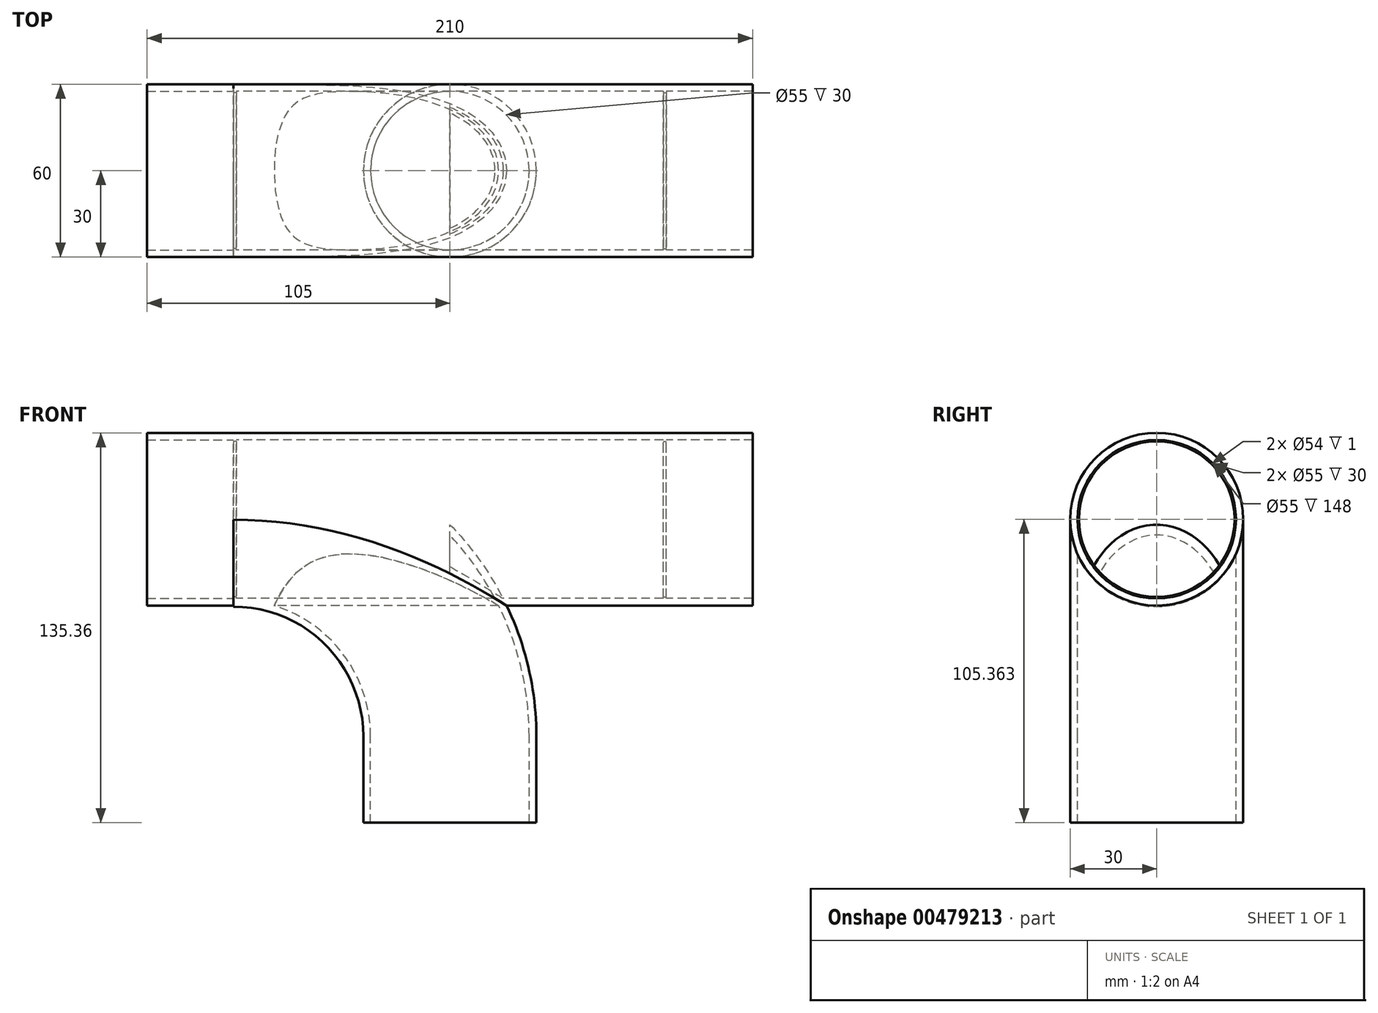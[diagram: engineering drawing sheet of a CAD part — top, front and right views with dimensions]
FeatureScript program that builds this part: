
annotation { "Feature Type Name" : "Feature", "Feature Type Description" : "" }
export const myFeature = defineFeature(function(context is Context, id is Id, definition is map)
    precondition{}
    {
        {
            var Q0;
            Q0=qCreatedBy(makeId("Top.planeOp"),FACE);
            var sketch = newSketch(context, id + "F0", { "sketchPlane" : qUnion([Q0])});
            skCircle(sketch, "E0", {"center": v(0, 0) * mm, "radius": 27.5 * mm});
            skCircle(sketch, "E1", {"center": v(0, 0) * mm, "radius": 30 * mm});
            skSolve(sketch);
        }
        {
            var Q0;
            Q0=qCreatedBy(makeId("Front.planeOp"),FACE);
            var sketch = newSketch(context, id + "F1", { "sketchPlane" : qUnion([Q0])});
            skArc(sketch, "E2", {"start": v(75, 75) * mm, "mid": v(21.97, 53.03) * mm, "end": v(0, 0) * mm});
            skLineSegment(sketch, "E3", {"start": v(0, 0) * mm, "end": v(75, 0) * mm});
            skLineSegment(sketch, "E4", {"start": v(75, 0) * mm, "end": v(75, 75) * mm});
            skLineSegment(sketch, "E5", {"start": v(0, 0) * mm, "end": v(-75, 0) * mm});
            skArc(sketch, "E6", {"start": v(0, 0) * mm, "mid": v(-21.97, 53.03) * mm, "end": v(-75, 75) * mm});
            skLineSegment(sketch, "E7", {"start": v(-75, 0) * mm, "end": v(-75, 75) * mm});
            skLineSegment(sketch, "E8", {"start": v(-75, 75) * mm, "end": v(75, 75) * mm});
            skSolve(sketch);
        }
        {
            var Q0;
            Q0=makeQuery(id+"F0.imprint","IMPRINT",FACE,{"disambiguationData":[TD([[makeQuery(id+"F0.imprint","IMPRINT",EDGE,{"derivedFrom":sQuery(id+"F0.wireOp",EDGE,"E0")}),-1.0]])]});
            var Q1;
            Q1=sQuery(id+"F1.wireOp",EDGE,"E6");
            sweep(context, id + "F2", {"profiles" : qUnion([Q0]), "path" : qUnion([Q1])});
        }
        {
            var Q0;
            Q0=qCreatedBy(makeId("Right.planeOp"),FACE);
            var sketch = newSketch(context, id + "F3", { "sketchPlane" : qUnion([Q0])});
            skCircle(sketch, "E9", {"center": v(0, 75.36) * mm, "radius": 30 * mm});
            skCircle(sketch, "E10", {"center": v(0, 75.36) * mm, "radius": 27.5 * mm});
            skSolve(sketch);
        }
        {
            var Q0;
            Q0=makeQuery(id+"F3.imprint","IMPRINT",FACE,{"disambiguationData":[TD([[makeQuery(id+"F3.imprint","IMPRINT",EDGE,{"derivedFrom":sQuery(id+"F3.wireOp",EDGE,"E9")}),1.0]])]});
            extrude(context, id + "F4", {"entities" : qUnion([Q0]), "operationType" : NewBodyOperationType.ADD, "depth" : 150 * mm, "offsetDistance" : 25 * mm, "symmetric" : true});
        }
        {
            var Q0;
            Q0=makeQuery(id+"F3.imprint","IMPRINT",FACE,{"disambiguationData":[TD([[makeQuery(id+"F3.imprint","IMPRINT",EDGE,{"derivedFrom":sQuery(id+"F3.wireOp",EDGE,"E10")}),1.0]])]});
            extrude(context, id + "F5", {"entities" : qUnion([Q0]), "operationType" : NewBodyOperationType.REMOVE, "oppositeDirection" : true, "depth" : 115 * mm, "offsetDistance" : 25 * mm});
        }
        {
            var Q0;
            Q0=makeQuery(id+"F2.opSweep","CAP_FACE",FACE,{"disambiguationData":[OSD([sQuery(id+"F0.wireOp",EDGE,"E0"),sQuery(id+"F0.wireOp",EDGE,"E1"),sQuery(id+"F1.wireOp",VERTEX,"E6.start")])],"isStart":true});
            extrude(context, id + "F6", {"entities" : qUnion([Q0]), "operationType" : NewBodyOperationType.ADD, "depth" : 30 * mm, "offsetDistance" : 25 * mm});
        }
        {
            var Q0;
            Q0=makeQuery(id+"F4.opExtrude","CAP_FACE",FACE,{"disambiguationData":[OSD([sQuery(id+"F3.wireOp",EDGE,"E9"),sQuery(id+"F3.wireOp",EDGE,"E10")])],"isStart":false});
            var sketch = newSketch(context, id + "F7", { "sketchPlane" : qUnion([Q0])});
            skCircle(sketch, "E11", {"center": v(0, 75.36) * mm, "radius": 27.5 * mm});
            skCircle(sketch, "E12", {"center": v(0, 75.36) * mm, "radius": 27 * mm});
            skSolve(sketch);
        }
        {
            var Q0;
            Q0=makeQuery(id+"F7.imprint","IMPRINT",FACE,{"disambiguationData":[TD([[makeQuery(id+"F7.imprint","IMPRINT",EDGE,{"derivedFrom":sQuery(id+"F7.wireOp",EDGE,"E11")}),1.0]])]});
            extrude(context, id + "F8", {"entities" : qUnion([Q0]), "operationType" : NewBodyOperationType.ADD, "oppositeDirection" : true, "depth" : 1 * mm, "offsetDistance" : 25 * mm});
        }
        {
            var Q0;
            Q0=makeQuery(id+"F8.boolean.opBoolean","MERGE",FACE,{"derivedFrom":[makeQuery(id+"F4.opExtrude","CAP_FACE",FACE,{"disambiguationData":[OSD([sQuery(id+"F3.wireOp",EDGE,"E9"),sQuery(id+"F3.wireOp",EDGE,"E10")])],"isStart":false}),makeQuery(id+"F8.opExtrude","CAP_FACE",FACE,{"disambiguationData":[OSD([sQuery(id+"F7.wireOp",EDGE,"E11"),sQuery(id+"F7.wireOp",EDGE,"E12")])],"isStart":true})]});
            var sketch = newSketch(context, id + "F9", { "sketchPlane" : qUnion([Q0])});
            skCircle(sketch, "E13", {"center": v(0, 75.36) * mm, "radius": 27.5 * mm});
            skCircle(sketch, "E14", {"center": v(0, 75.36) * mm, "radius": 30 * mm});
            skSolve(sketch);
        }
        {
            var Q0;
            Q0=makeQuery(id+"F9.imprint","IMPRINT",FACE,{"disambiguationData":[TD([[makeQuery(id+"F9.imprint","IMPRINT",EDGE,{"derivedFrom":sQuery(id+"F9.wireOp",EDGE,"E13")}),-1.0]])]});
            extrude(context, id + "F10", {"entities" : qUnion([Q0]), "operationType" : NewBodyOperationType.ADD, "depth" : 30 * mm, "offsetDistance" : 25 * mm});
        }
        {
            var Q0;
            Q0=makeQuery(id+"F4.boolean.opBoolean","MERGE",FACE,{"derivedFrom":[makeQuery(id+"F2.opSweep","CAP_FACE",FACE,{"disambiguationData":[OSD([sQuery(id+"F0.wireOp",EDGE,"E0"),sQuery(id+"F0.wireOp",EDGE,"E1"),sQuery(id+"F1.wireOp",VERTEX,"E6.end")])],"isStart":false}),makeQuery(id+"F4.opExtrude","CAP_FACE",FACE,{"disambiguationData":[OSD([sQuery(id+"F3.wireOp",EDGE,"E9"),sQuery(id+"F3.wireOp",EDGE,"E10")])],"isStart":true})]});
            var sketch = newSketch(context, id + "F11", { "sketchPlane" : qUnion([Q0])});
            skCircle(sketch, "E15", {"center": v(0, 75.36) * mm, "radius": 27.5 * mm});
            skCircle(sketch, "E16", {"center": v(0, 75.36) * mm, "radius": 27 * mm});
            skCircle(sketch, "E17", {"center": v(0, 75.36) * mm, "radius": 30 * mm});
            skSolve(sketch);
        }
        {
            var Q0;
            Q0=makeQuery(id+"F11.imprint","IMPRINT",FACE,{"disambiguationData":[TD([[makeQuery(id+"F11.imprint","IMPRINT",EDGE,{"derivedFrom":sQuery(id+"F11.wireOp",EDGE,"E15")}),-1.0]])]});
            extrude(context, id + "F12", {"entities" : qUnion([Q0]), "operationType" : NewBodyOperationType.ADD, "oppositeDirection" : true, "depth" : 1 * mm, "offsetDistance" : 25 * mm});
        }
        {
            var Q0;
            Q0=makeQuery(id+"F11.imprint","IMPRINT",FACE,{"disambiguationData":[TD([[makeQuery(id+"F11.imprint","IMPRINT",EDGE,{"derivedFrom":sQuery(id+"F11.wireOp",EDGE,"E15")}),1.0]])]});
            extrude(context, id + "F13", {"entities" : qUnion([Q0]), "operationType" : NewBodyOperationType.ADD, "depth" : 30 * mm, "offsetDistance" : 25 * mm});
        }
    });
